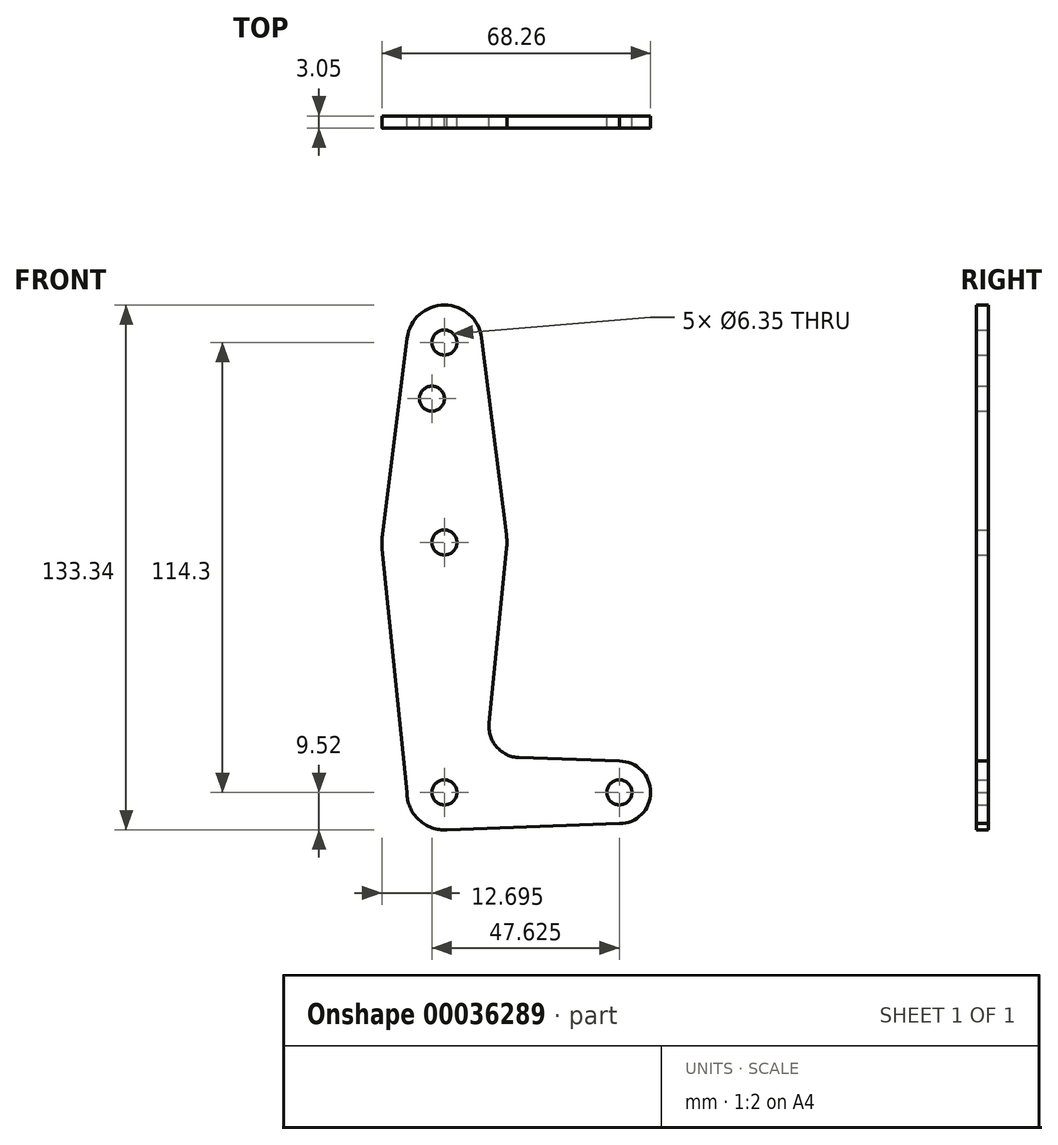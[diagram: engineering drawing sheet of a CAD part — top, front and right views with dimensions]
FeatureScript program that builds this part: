
annotation { "Feature Type Name" : "Feature", "Feature Type Description" : "" }
export const myFeature = defineFeature(function(context is Context, id is Id, definition is map)
    precondition{}
    {
        {
            var Q0;
            Q0=qCreatedBy(makeId("Front.planeOp"),FACE);
            var sketch = newSketch(context, id + "F0", { "sketchPlane" : qUnion([Q0])});
            skCircle(sketch, "E0", {"center": v(0, -63.5) * mm, "radius": 9.53 * mm});
            skCircle(sketch, "E1", {"center": v(0, 0) * mm, "radius": 15.88 * mm});
            skCircle(sketch, "E2", {"center": v(0, 50.8) * mm, "radius": 9.53 * mm});
            skCircle(sketch, "E3", {"center": v(44.45, -63.5) * mm, "radius": 7.94 * mm});
            skLineSegment(sketch, "E4", {"start": v(0, 50.8) * mm, "end": v(0, 0) * mm, "construction": true});
            skLineSegment(sketch, "E5", {"start": v(0, 0) * mm, "end": v(0, -63.5) * mm, "construction": true});
            skLineSegment(sketch, "E6", {"start": v(0, -63.5) * mm, "end": v(44.45, -63.5) * mm, "construction": true});
            skLineSegment(sketch, "E7", {"start": v(-15.96, 0) * mm, "end": v(-9.52, -63.5) * mm});
            skLineSegment(sketch, "E8", {"start": v(15.95, 0) * mm, "end": v(11.34, -45.9) * mm});
            skLineSegment(sketch, "E9", {"start": v(18.97, -54.65) * mm, "end": v(44.45, -55.56) * mm});
            skLineSegment(sketch, "E10", {"start": v(0, -73.02) * mm, "end": v(44.45, -71.44) * mm});
            skCircle(sketch, "E11", {"center": v(0, 50.8) * mm, "radius": 3.18 * mm});
            skCircle(sketch, "E12", {"center": v(-3.17, 36.53) * mm, "radius": 3.18 * mm});
            skCircle(sketch, "E13", {"center": v(0, 0) * mm, "radius": 3.18 * mm});
            skCircle(sketch, "E14", {"center": v(0, -63.5) * mm, "radius": 3.18 * mm});
            skCircle(sketch, "E15", {"center": v(44.45, -63.5) * mm, "radius": 3.18 * mm});
            skPoint(sketch, "E16.newPointA", {"position": v(9.57, -63.5) * mm});
            skArc(sketch, "E16.filletArc", {"start": v(11.34, -45.9) * mm, "mid": v(13.26, -51.93) * mm, "end": v(18.97, -54.65) * mm});
            skLineSegment(sketch, "E17", {"start": v(-9.45, 52) * mm, "end": v(-15.75, 1.98) * mm});
            skLineSegment(sketch, "E18", {"start": v(9.45, 52) * mm, "end": v(15.75, 1.98) * mm});
            skSolve(sketch);
        }
        {
            var Q0;
            Q0 = qSketchRegion(id + "F0", true);
            extrude(context, id + "F1", {"entities" : qUnion([Q0]), "depth" : 3.05 * mm});
        }
    });
